# Revit family: Channel-Unistrut-P5000_T
name_source: partatom
category: Specialty Equipment
revit_build: Autodesk Revit Architecture 2012 (Build: 20110309_2315(x64)
units: mm (PartAtom-declared; Revit-internal decimal feet)

## types (1)
- P5000 T
    04 CSI = 26 05 48
    95 CSI = 16070
    Assembly Code = D5020100
    CAD URL = http://unistrut.us
    CSI MasterSpec = http://www.unistrut.us
    Category = Specialty Equipment
    Construction Note = Slots are 11⁄8" x 9⁄16" @ 2" on Center
    Description = P5000 T Channel
    Gauge Thickness = 12 Gauge (.105”)
    Hole Spacing On Center Dimension = 2"
    Knockouts Spacing From End = 1"
    Literature URL = http://unistrut.us
    Load Capacity Note = Visit the product page for load application and capacity.
    Manufacturer = Unistrut by Atkore International
    Manufacturer Fax = 708-339-7814
    Material = Multiple Options - See Catalog
    Model = P5000 T
    Overall Height = 3 1/4"
    Overall Width = 1 5/8"
    Part Type = Channel
    Power Strut Part Number = PS 200 KO6
    Product Page URL = http://unistrut.us
    Subcategory = 1 5/8" Channels
    URL = http://unistrut.us
    Unit = <By Category>
    Weight Per Foot = 3.00 lb/ft

## geometry (parser evidence)
native form markers: Sweep x10
no freeform markers — native parametric forms only
